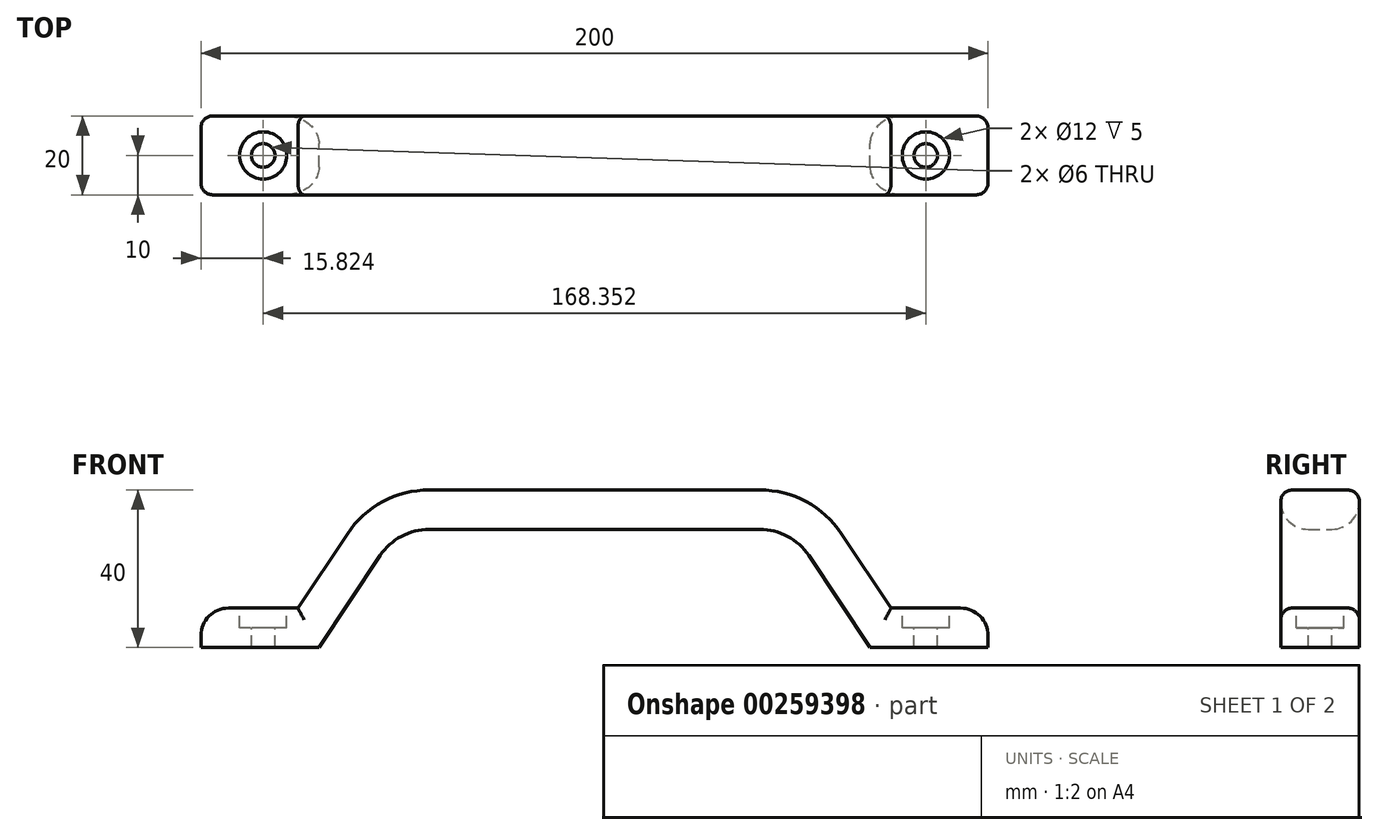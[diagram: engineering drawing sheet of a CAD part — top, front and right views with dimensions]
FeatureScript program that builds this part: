
annotation { "Feature Type Name" : "Feature", "Feature Type Description" : "" }
export const myFeature = defineFeature(function(context is Context, id is Id, definition is map)
    precondition{}
    {
        {
            var Q0;
            Q0=qCreatedBy(makeId("Front.planeOp"),FACE);
            var sketch = newSketch(context, id + "F0", { "sketchPlane" : qUnion([Q0])});
            skLineSegment(sketch, "E0", {"start": v(0, 30) * mm, "end": v(41.97, 30) * mm});
            skLineSegment(sketch, "E1", {"start": v(54.45, 23.32) * mm, "end": v(70, 0) * mm});
            skLineSegment(sketch, "E2", {"start": v(70, 0) * mm, "end": v(100, 0) * mm});
            skLineSegment(sketch, "E3", {"start": v(0, 30) * mm, "end": v(0, 0) * mm, "construction": true});
            skPoint(sketch, "E4.visualSharp", {"position": v(50, 30) * mm});
            skArc(sketch, "E4.filletArc", {"start": v(54.45, 23.32) * mm, "mid": v(49.05, 28.23) * mm, "end": v(41.97, 30) * mm});
            skLineSegment(sketch, "E5.0", {"start": v(75.35, 10) * mm, "end": v(100, 10) * mm});
            skLineSegment(sketch, "E5.1", {"start": v(62.77, 28.87) * mm, "end": v(75.35, 10) * mm});
            skArc(sketch, "E5.2", {"start": v(62.77, 28.87) * mm, "mid": v(53.77, 37.04) * mm, "end": v(41.97, 40) * mm});
            skLineSegment(sketch, "E5.3", {"start": v(0, 40) * mm, "end": v(41.97, 40) * mm});
            skLineSegment(sketch, "E6", {"start": v(100, 10) * mm, "end": v(100, 0) * mm});
            skLineSegment(sketch, "E7.MirrorCS", {"start": v(0, 30) * mm, "end": v(-41.97, 30) * mm});
            skArc(sketch, "E8.MirrorCS", {"start": v(-54.45, 23.32) * mm, "mid": v(-49.05, 28.23) * mm, "end": v(-41.97, 30) * mm});
            skLineSegment(sketch, "E9.MirrorCS", {"start": v(-54.45, 23.32) * mm, "end": v(-70, 0) * mm});
            skLineSegment(sketch, "E10.MirrorCS", {"start": v(-70, 0) * mm, "end": v(-100, 0) * mm});
            skLineSegment(sketch, "E11.MirrorCS", {"start": v(-100, 10) * mm, "end": v(-100, 0) * mm});
            skLineSegment(sketch, "E12.MirrorCS", {"start": v(-75.35, 10) * mm, "end": v(-100, 10) * mm});
            skLineSegment(sketch, "E13.MirrorCS", {"start": v(-62.77, 28.87) * mm, "end": v(-75.35, 10) * mm});
            skArc(sketch, "E14.MirrorCS", {"start": v(-62.77, 28.87) * mm, "mid": v(-53.77, 37.04) * mm, "end": v(-41.97, 40) * mm});
            skLineSegment(sketch, "E15.MirrorCS", {"start": v(0, 40) * mm, "end": v(-41.97, 40) * mm});
            skSolve(sketch);
        }
        {
            var Q0;
            Q0 = qSketchRegion(id + "F0", true);
            extrude(context, id + "F1", {"entities" : qUnion([Q0]), "depth" : 20 * mm});
        }
        {
            var Q0;
            Q0=makeQuery(id+"F1.opExtrude","SWEPT_EDGE",EDGE,{"disambiguationData":[OSD([sQuery(id+"F0.wireOp",EDGE,"E11.MirrorCS"),sQuery(id+"F0.wireOp",EDGE,"E12.MirrorCS")])]});
            var Q1;
            Q1=makeQuery(id+"F1.opExtrude","SWEPT_EDGE",EDGE,{"disambiguationData":[OSD([sQuery(id+"F0.wireOp",EDGE,"E5.0"),sQuery(id+"F0.wireOp",EDGE,"E6")])]});
            fillet(context, id + "F2", {"entities" : qUnion([Q0, Q1]), "radius" : 7 * mm, "tangentPropagation" : true, "allowEdgeOverflow" : false});
        }
        {
            var Q0;
            Q0=makeQuery(id+"F1.opExtrude","CAP_EDGE",EDGE,{"disambiguationData":[OSD([sQuery(id+"F0.wireOp",EDGE,"E12.MirrorCS")])],"isStart":false});
            var Q1;
            Q1=makeQuery(id+"F1.opExtrude","CAP_EDGE",EDGE,{"disambiguationData":[OSD([sQuery(id+"F0.wireOp",EDGE,"E12.MirrorCS")])],"isStart":true});
            var Q2;
            Q2=makeQuery(id+"F1.opExtrude","CAP_EDGE",EDGE,{"disambiguationData":[OSD([sQuery(id+"F0.wireOp",EDGE,"E13.MirrorCS")])],"isStart":true});
            var Q3;
            Q3=makeQuery(id+"F1.opExtrude","CAP_EDGE",EDGE,{"disambiguationData":[OSD([sQuery(id+"F0.wireOp",EDGE,"E13.MirrorCS")])],"isStart":false});
            var Q4;
            Q4=makeQuery(id+"F1.opExtrude","CAP_EDGE",EDGE,{"disambiguationData":[OSD([sQuery(id+"F0.wireOp",EDGE,"E5.0")])],"isStart":false});
            var Q5;
            Q5=makeQuery(id+"F1.opExtrude","CAP_EDGE",EDGE,{"disambiguationData":[OSD([sQuery(id+"F0.wireOp",EDGE,"E5.0")])],"isStart":true});
            fillet(context, id + "F3", {"entities" : qUnion([Q0, Q1, Q2, Q3, Q4, Q5]), "radius" : 3 * mm, "tangentPropagation" : true, "allowEdgeOverflow" : false});
        }
        {
            var Q0;
            Q0=makeQuery(id+"F1.opExtrude","CAP_EDGE",EDGE,{"disambiguationData":[OSD([sQuery(id+"F0.wireOp",EDGE,"E9.MirrorCS")])],"isStart":false});
            var Q1;
            Q1=makeQuery(id+"F1.opExtrude","CAP_EDGE",EDGE,{"disambiguationData":[OSD([sQuery(id+"F0.wireOp",EDGE,"E9.MirrorCS")])],"isStart":true});
            fillet(context, id + "F4", {"entities" : qUnion([Q0, Q1]), "radius" : 7 * mm, "tangentPropagation" : true, "allowEdgeOverflow" : false});
        }
        {
            var Q0;
            Q0=makeQuery(id+"F1.opExtrude","SWEPT_FACE",FACE,{"disambiguationData":[OSD([sQuery(id+"F0.wireOp",EDGE,"E12.MirrorCS")])]});
            var sketch = newSketch(context, id + "F5", { "sketchPlane" : qUnion([Q0])});
            skLineSegment(sketch, "E16.0", {"start": v(-93, -3) * mm, "end": v(-93, -17) * mm, "construction": true});
            skLineSegment(sketch, "E16.1", {"start": v(-75.35, -17) * mm, "end": v(-75.35, -3) * mm, "construction": true});
            skLineSegment(sketch, "E16.2", {"start": v(75.35, -17) * mm, "end": v(75.35, -3) * mm, "construction": true});
            skLineSegment(sketch, "E16.3", {"start": v(93, -17) * mm, "end": v(93, -3) * mm, "construction": true});
            skPoint(sketch, "E17", {"position": v(-84.18, -10) * mm});
            skPoint(sketch, "E18", {"position": v(84.18, -10) * mm});
            skCircle(sketch, "E19", {"center": v(-84.18, -10) * mm, "radius": 3 * mm});
            skCircle(sketch, "E20", {"center": v(-84.18, -10) * mm, "radius": 6 * mm});
            skCircle(sketch, "E21", {"center": v(84.18, -10) * mm, "radius": 6 * mm});
            skCircle(sketch, "E22", {"center": v(84.18, -10) * mm, "radius": 3 * mm});
            skSolve(sketch);
        }
        {
            var Q0;
            Q0 = qSketchRegion(id + "F5", true);
            extrude(context, id + "F6", {"entities" : qUnion([Q0]), "operationType" : NewBodyOperationType.REMOVE, "oppositeDirection" : true, "depth" : 5 * mm});
        }
        {
            var Q0;
            Q0=makeQuery(id+"F6.boolean.opBoolean","SPLIT",FACE,{"disambiguationData":[TD([makeQuery(id+"F6.opExtrude","SWEPT_FACE",FACE,{"disambiguationData":[OSD([sQuery(id+"F5.wireOp",EDGE,"E19")])]})])],"derivedFrom":makeQuery(id+"F1.opExtrude","SWEPT_FACE",FACE,{"disambiguationData":[OSD([sQuery(id+"F0.wireOp",EDGE,"E12.MirrorCS")])]})});
            var Q1;
            Q1=makeQuery(id+"F6.boolean.opBoolean","SPLIT",FACE,{"disambiguationData":[TD([makeQuery(id+"F6.opExtrude","SWEPT_FACE",FACE,{"disambiguationData":[OSD([sQuery(id+"F5.wireOp",EDGE,"E22")])]})])],"derivedFrom":makeQuery(id+"F1.opExtrude","SWEPT_FACE",FACE,{"disambiguationData":[OSD([sQuery(id+"F0.wireOp",EDGE,"E5.0")])]})});
            extrude(context, id + "F7", {"entities" : qUnion([Q0, Q1]), "operationType" : NewBodyOperationType.REMOVE, "oppositeDirection" : true, "depth" : 25 * mm});
        }
    });
